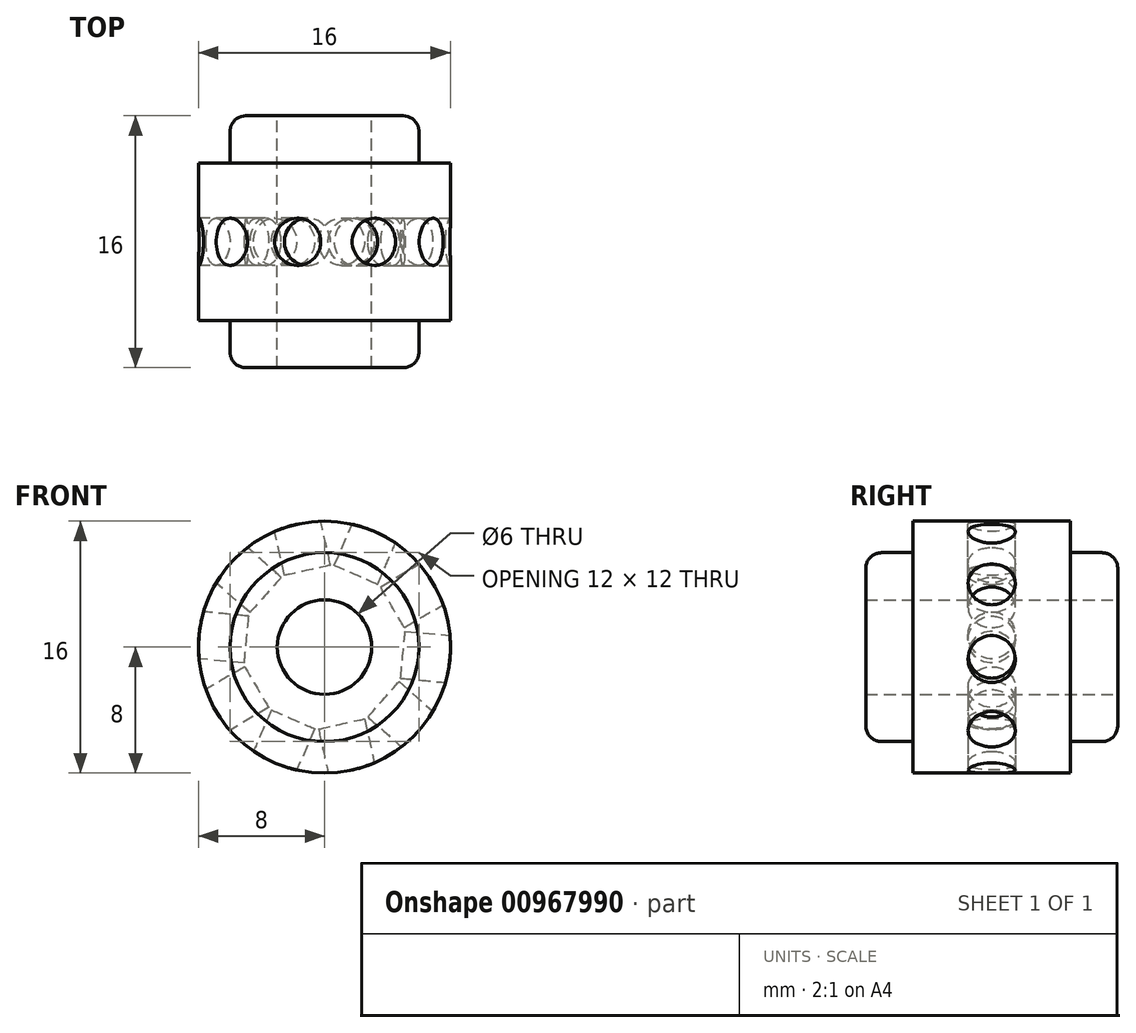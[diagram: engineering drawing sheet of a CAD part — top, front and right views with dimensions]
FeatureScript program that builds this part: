
annotation { "Feature Type Name" : "Feature", "Feature Type Description" : "" }
export const myFeature = defineFeature(function(context is Context, id is Id, definition is map)
    precondition{}
    {
        {
            var Q0;
            Q0=qCreatedBy(makeId("Front.planeOp"),FACE);
            var sketch = newSketch(context, id + "F0", { "sketchPlane" : qUnion([Q0])});
            skCircle(sketch, "E0", {"center": v(0, 0) * mm, "radius": 8 * mm});
            skSolve(sketch);
        }
        {
            var Q0;
            Q0=makeQuery(id+"F0.imprint","IMPRINT",FACE,{"disambiguationData":[TD([[makeQuery(id+"F0.imprint","IMPRINT",EDGE,{"derivedFrom":sQuery(id+"F0.wireOp",EDGE,"E0")}),1.0]])]});
            extrude(context, id + "F1", {"entities" : qUnion([Q0]), "depth" : 10 * mm, "offsetDistance" : 25 * mm});
        }
        {
            var Q0;
            Q0=makeQuery(id+"F1.opExtrude","CAP_FACE",FACE,{"disambiguationData":[OSD([sQuery(id+"F0.wireOp",EDGE,"E0")])],"isStart":true});
            var sketch = newSketch(context, id + "F2", { "sketchPlane" : qUnion([Q0])});
            skCircle(sketch, "E1", {"center": v(0, 0) * mm, "radius": 6 * mm});
            skSolve(sketch);
        }
        {
            var Q0;
            Q0=makeQuery(id+"F2.imprint","IMPRINT",FACE,{"disambiguationData":[TD([[makeQuery(id+"F2.imprint","IMPRINT",EDGE,{"derivedFrom":sQuery(id+"F2.wireOp",EDGE,"E1")}),1.0]])]});
            extrude(context, id + "F3", {"entities" : qUnion([Q0]), "operationType" : NewBodyOperationType.ADD, "oppositeDirection" : true, "depth" : 13 * mm, "offsetDistance" : 25 * mm, "hasSecondDirection" : true, "secondDirectionOppositeDirection" : false, "secondDirectionDepth" : 3 * mm});
        }
        {
            var Q0;
            Q0=qCreatedBy(makeId("Front.planeOp"),FACE);
            var sketch = newSketch(context, id + "F4", { "sketchPlane" : qUnion([Q0])});
            skCircle(sketch, "E2.cCircle", {"center": v(0, 0) * mm, "radius": 8 * mm, "construction": true});
            skLineSegment(sketch, "E2.0", {"start": v(-5.57, -6.3) * mm, "end": v(-8.21, -1.82) * mm});
            skLineSegment(sketch, "E2.1", {"start": v(-8.21, -1.82) * mm, "end": v(-7.71, 3.36) * mm});
            skLineSegment(sketch, "E2.2", {"start": v(-7.71, 3.36) * mm, "end": v(-4.27, 7.25) * mm});
            skLineSegment(sketch, "E2.3", {"start": v(-4.27, 7.25) * mm, "end": v(0.8, 8.37) * mm});
            skLineSegment(sketch, "E2.4", {"start": v(0.8, 8.37) * mm, "end": v(5.57, 6.3) * mm});
            skLineSegment(sketch, "E2.5", {"start": v(5.57, 6.3) * mm, "end": v(8.21, 1.82) * mm});
            skLineSegment(sketch, "E2.6", {"start": v(8.21, 1.82) * mm, "end": v(7.71, -3.36) * mm});
            skLineSegment(sketch, "E2.7", {"start": v(7.71, -3.36) * mm, "end": v(4.27, -7.25) * mm});
            skLineSegment(sketch, "E2.8", {"start": v(4.27, -7.25) * mm, "end": v(-0.8, -8.37) * mm});
            skLineSegment(sketch, "E2.9", {"start": v(-0.8, -8.37) * mm, "end": v(-5.57, -6.3) * mm});
            skPoint(sketch, "E2.0.midPoint", {"position": v(-6.9, -4.06) * mm});
            skSolve(sketch);
        }
        {
            var Q0;
            Q0=makeQuery(id+"F4.imprint","IMPRINT",FACE,{"disambiguationData":[TD([[makeQuery(id+"F4.imprint","IMPRINT",EDGE,{"derivedFrom":sQuery(id+"F4.wireOp",EDGE,"E2.0")}),-1.0]])]});
            extrude(context, id + "F5", {"entities" : qUnion([Q0]), "operationType" : NewBodyOperationType.ADD, "depth" : 10 * mm, "offsetDistance" : 25 * mm});
        }
        {
            var Q0;
            Q0=makeQuery(id+"F5.opExtrude","SWEPT_FACE",FACE,{"disambiguationData":[OSD([sQuery(id+"F4.wireOp",EDGE,"E2.3")])]});
            var sketch = newSketch(context, id + "F6", { "sketchPlane" : qUnion([Q0])});
            skCircle(sketch, "E3", {"center": v(0, -5) * mm, "radius": 1.5 * mm});
            skSolve(sketch);
        }
        {
            var Q0;
            Q0=makeQuery(id+"F5.opExtrude","SWEPT_FACE",FACE,{"disambiguationData":[OSD([sQuery(id+"F4.wireOp",EDGE,"E2.2")])]});
            var sketch = newSketch(context, id + "F7", { "sketchPlane" : qUnion([Q0])});
            skCircle(sketch, "E4", {"center": v(5, 0) * mm, "radius": 1.5 * mm});
            skSolve(sketch);
        }
        {
            var Q0;
            Q0=makeQuery(id+"F5.opExtrude","SWEPT_FACE",FACE,{"disambiguationData":[OSD([sQuery(id+"F4.wireOp",EDGE,"E2.1")])]});
            var sketch = newSketch(context, id + "F8", { "sketchPlane" : qUnion([Q0])});
            skCircle(sketch, "E5", {"center": v(5, 0) * mm, "radius": 1.5 * mm});
            skSolve(sketch);
        }
        {
            var Q0;
            Q0=makeQuery(id+"F5.opExtrude","SWEPT_FACE",FACE,{"disambiguationData":[OSD([sQuery(id+"F4.wireOp",EDGE,"E2.0")])]});
            var sketch = newSketch(context, id + "F9", { "sketchPlane" : qUnion([Q0])});
            skCircle(sketch, "E6", {"center": v(5, 0) * mm, "radius": 1.5 * mm});
            skSolve(sketch);
        }
        {
            var Q0;
            Q0=makeQuery(id+"F5.opExtrude","SWEPT_FACE",FACE,{"disambiguationData":[OSD([sQuery(id+"F4.wireOp",EDGE,"E2.9")])]});
            var sketch = newSketch(context, id + "F10", { "sketchPlane" : qUnion([Q0])});
            skCircle(sketch, "E7", {"center": v(0, 5) * mm, "radius": 1.5 * mm});
            skSolve(sketch);
        }
        {
            var Q0;
            Q0=makeQuery(id+"F5.opExtrude","SWEPT_FACE",FACE,{"disambiguationData":[OSD([sQuery(id+"F4.wireOp",EDGE,"E2.8")])]});
            var sketch = newSketch(context, id + "F11", { "sketchPlane" : qUnion([Q0])});
            skCircle(sketch, "E8", {"center": v(0, 5) * mm, "radius": 1.5 * mm});
            skSolve(sketch);
        }
        {
            var Q0;
            Q0=makeQuery(id+"F5.opExtrude","SWEPT_FACE",FACE,{"disambiguationData":[OSD([sQuery(id+"F4.wireOp",EDGE,"E2.7")])]});
            var sketch = newSketch(context, id + "F12", { "sketchPlane" : qUnion([Q0])});
            skCircle(sketch, "E9", {"center": v(-5, 0) * mm, "radius": 1.5 * mm});
            skSolve(sketch);
        }
        {
            var Q0;
            Q0=makeQuery(id+"F5.opExtrude","SWEPT_FACE",FACE,{"disambiguationData":[OSD([sQuery(id+"F4.wireOp",EDGE,"E2.6")])]});
            var sketch = newSketch(context, id + "F13", { "sketchPlane" : qUnion([Q0])});
            skCircle(sketch, "E10", {"center": v(-5, 0) * mm, "radius": 1.5 * mm});
            skSolve(sketch);
        }
        {
            var Q0;
            Q0=makeQuery(id+"F5.opExtrude","SWEPT_FACE",FACE,{"disambiguationData":[OSD([sQuery(id+"F4.wireOp",EDGE,"E2.5")])]});
            var sketch = newSketch(context, id + "F14", { "sketchPlane" : qUnion([Q0])});
            skCircle(sketch, "E11", {"center": v(-5, 0) * mm, "radius": 1.5 * mm});
            skSolve(sketch);
        }
        {
            var Q0;
            Q0=makeQuery(id+"F5.opExtrude","SWEPT_FACE",FACE,{"disambiguationData":[OSD([sQuery(id+"F4.wireOp",EDGE,"E2.4")])]});
            var sketch = newSketch(context, id + "F15", { "sketchPlane" : qUnion([Q0])});
            skCircle(sketch, "E12", {"center": v(0, -5) * mm, "radius": 1.5 * mm});
            skSolve(sketch);
        }
        {
            var Q0;
            Q0=makeQuery(id+"F13.imprint","IMPRINT",FACE,{"disambiguationData":[TD([[makeQuery(id+"F13.imprint","IMPRINT",EDGE,{"derivedFrom":sQuery(id+"F13.wireOp",EDGE,"E10")}),1.0]])]});
            extrude(context, id + "F16", {"entities" : qUnion([Q0]), "operationType" : NewBodyOperationType.REMOVE, "oppositeDirection" : true, "depth" : 3 * mm, "offsetDistance" : 25 * mm});
        }
        {
            var Q0;
            Q0=makeQuery(id+"F14.imprint","IMPRINT",FACE,{"disambiguationData":[TD([[makeQuery(id+"F14.imprint","IMPRINT",EDGE,{"derivedFrom":sQuery(id+"F14.wireOp",EDGE,"E11")}),1.0]])]});
            extrude(context, id + "F17", {"entities" : qUnion([Q0]), "operationType" : NewBodyOperationType.REMOVE, "oppositeDirection" : true, "depth" : 3 * mm, "offsetDistance" : 25 * mm});
        }
        {
            var Q0;
            Q0=makeQuery(id+"F15.imprint","IMPRINT",FACE,{"disambiguationData":[TD([[makeQuery(id+"F15.imprint","IMPRINT",EDGE,{"derivedFrom":sQuery(id+"F15.wireOp",EDGE,"E12")}),1.0]])]});
            extrude(context, id + "F18", {"entities" : qUnion([Q0]), "operationType" : NewBodyOperationType.REMOVE, "oppositeDirection" : true, "depth" : 3 * mm, "offsetDistance" : 25 * mm});
        }
        {
            var Q0;
            Q0=makeQuery(id+"F6.imprint","IMPRINT",FACE,{"disambiguationData":[TD([[makeQuery(id+"F6.imprint","IMPRINT",EDGE,{"derivedFrom":sQuery(id+"F6.wireOp",EDGE,"E3")}),1.0]])]});
            extrude(context, id + "F19", {"entities" : qUnion([Q0]), "operationType" : NewBodyOperationType.REMOVE, "oppositeDirection" : true, "depth" : 3 * mm, "offsetDistance" : 25 * mm});
        }
        {
            var Q0;
            Q0=makeQuery(id+"F7.imprint","IMPRINT",FACE,{"disambiguationData":[TD([[makeQuery(id+"F7.imprint","IMPRINT",EDGE,{"derivedFrom":sQuery(id+"F7.wireOp",EDGE,"E4")}),1.0]])]});
            extrude(context, id + "F20", {"entities" : qUnion([Q0]), "operationType" : NewBodyOperationType.REMOVE, "oppositeDirection" : true, "depth" : 3 * mm, "offsetDistance" : 25 * mm});
        }
        {
            var Q0;
            Q0=makeQuery(id+"F8.imprint","IMPRINT",FACE,{"disambiguationData":[TD([[makeQuery(id+"F8.imprint","IMPRINT",EDGE,{"derivedFrom":sQuery(id+"F8.wireOp",EDGE,"E5")}),1.0]])]});
            extrude(context, id + "F21", {"entities" : qUnion([Q0]), "operationType" : NewBodyOperationType.REMOVE, "oppositeDirection" : true, "depth" : 3 * mm, "offsetDistance" : 25 * mm});
        }
        {
            var Q0;
            Q0=makeQuery(id+"F9.imprint","IMPRINT",FACE,{"disambiguationData":[TD([[makeQuery(id+"F9.imprint","IMPRINT",EDGE,{"derivedFrom":sQuery(id+"F9.wireOp",EDGE,"E6")}),1.0]])]});
            extrude(context, id + "F22", {"entities" : qUnion([Q0]), "operationType" : NewBodyOperationType.REMOVE, "oppositeDirection" : true, "depth" : 3 * mm, "offsetDistance" : 25 * mm});
        }
        {
            var Q0;
            Q0=makeQuery(id+"F10.imprint","IMPRINT",FACE,{"disambiguationData":[TD([[makeQuery(id+"F10.imprint","IMPRINT",EDGE,{"derivedFrom":sQuery(id+"F10.wireOp",EDGE,"E7")}),1.0]])]});
            extrude(context, id + "F23", {"entities" : qUnion([Q0]), "operationType" : NewBodyOperationType.REMOVE, "oppositeDirection" : true, "depth" : 3 * mm, "offsetDistance" : 25 * mm});
        }
        {
            var Q0;
            Q0=makeQuery(id+"F11.imprint","IMPRINT",FACE,{"disambiguationData":[TD([[makeQuery(id+"F11.imprint","IMPRINT",EDGE,{"derivedFrom":sQuery(id+"F11.wireOp",EDGE,"E8")}),1.0]])]});
            extrude(context, id + "F24", {"entities" : qUnion([Q0]), "operationType" : NewBodyOperationType.REMOVE, "oppositeDirection" : true, "depth" : 3 * mm, "offsetDistance" : 25 * mm});
        }
        {
            var Q0;
            Q0=makeQuery(id+"F12.imprint","IMPRINT",FACE,{"disambiguationData":[TD([[makeQuery(id+"F12.imprint","IMPRINT",EDGE,{"derivedFrom":sQuery(id+"F12.wireOp",EDGE,"E9")}),1.0]])]});
            extrude(context, id + "F25", {"entities" : qUnion([Q0]), "operationType" : NewBodyOperationType.REMOVE, "oppositeDirection" : true, "depth" : 3 * mm, "offsetDistance" : 25 * mm});
        }
        {
            var Q0;
            Q0=makeQuery(id+"F3.opExtrude","CAP_FACE",FACE,{"disambiguationData":[OSD([sQuery(id+"F2.wireOp",EDGE,"E1")])],"isStart":true});
            var sketch = newSketch(context, id + "F26", { "sketchPlane" : qUnion([Q0])});
            skCircle(sketch, "E13", {"center": v(0, 0) * mm, "radius": 3 * mm});
            skSolve(sketch);
        }
        {
            var Q0;
            Q0=makeQuery(id+"F26.imprint","IMPRINT",FACE,{"disambiguationData":[TD([[makeQuery(id+"F26.imprint","IMPRINT",EDGE,{"derivedFrom":sQuery(id+"F26.wireOp",EDGE,"E13")}),1.0]])]});
            extrude(context, id + "F27", {"entities" : qUnion([Q0]), "operationType" : NewBodyOperationType.REMOVE, "oppositeDirection" : true, "depth" : 16 * mm, "offsetDistance" : 25 * mm});
        }
        {
            var Q0;
            Q0=qCreatedBy(makeId("Front.planeOp"),FACE);
            var sketch = newSketch(context, id + "F28", { "sketchPlane" : qUnion([Q0])});
            skCircle(sketch, "E14", {"center": v(0, 0) * mm, "radius": 8 * mm});
            skCircle(sketch, "E15", {"center": v(0, 0) * mm, "radius": 9.27 * mm});
            skSolve(sketch);
        }
        {
            var Q0;
            Q0=makeQuery(id+"F28.imprint","IMPRINT",FACE,{"disambiguationData":[TD([[makeQuery(id+"F28.imprint","IMPRINT",EDGE,{"derivedFrom":sQuery(id+"F28.wireOp",EDGE,"E14")}),-1.0]])]});
            extrude(context, id + "F29", {"entities" : qUnion([Q0]), "operationType" : NewBodyOperationType.REMOVE, "depth" : 10 * mm, "offsetDistance" : 25 * mm});
        }
        {
            var Q0;
            Q0=makeQuery(id+"F29.boolean.opBoolean","COPY",EDGE,{"derivedFrom":makeQuery(id+"F29.opExtrude","CAP_EDGE",EDGE,{"disambiguationData":[OSD([sQuery(id+"F28.wireOp",EDGE,"E14")])],"isStart":false})});
            var Q1;
            Q1=makeQuery(id+"F3.opExtrude","CAP_EDGE",EDGE,{"disambiguationData":[OSD([sQuery(id+"F2.wireOp",EDGE,"E1")])],"isStart":false});
            var Q2;
            Q2=makeQuery(id+"F29.boolean.opBoolean","COPY",EDGE,{"derivedFrom":makeQuery(id+"F29.opExtrude","CAP_EDGE",EDGE,{"disambiguationData":[OSD([sQuery(id+"F28.wireOp",EDGE,"E14")])],"isStart":true})});
            var Q3;
            Q3=makeQuery(id+"F3.opExtrude","CAP_EDGE",EDGE,{"disambiguationData":[OSD([sQuery(id+"F2.wireOp",EDGE,"E1")])],"isStart":true});
            fillet(context, id + "F30", {"entities" : qUnion([Q0, Q1, Q2, Q3]), "radius" : 1 * mm, "tangentPropagation" : true, "allowEdgeOverflow" : false});
        }
    });
